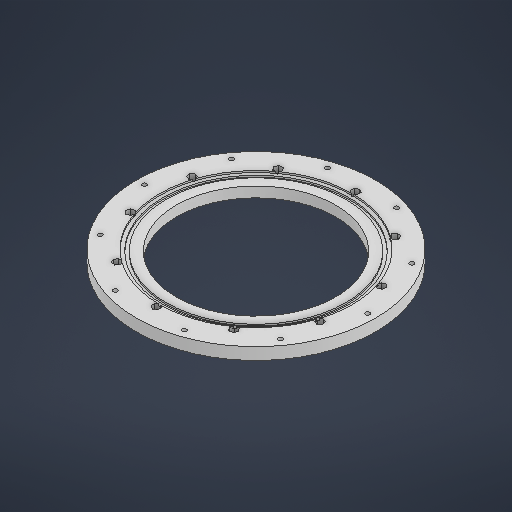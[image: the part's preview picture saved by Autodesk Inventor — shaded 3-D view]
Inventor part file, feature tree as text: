
AUTODESK INVENTOR PART (.ipt)
format: ipt  version: 2025 (Build 290162000, 162)  size: 542,720 bytes
history: native  units: in
note: dims shown in document units (in); Inventor stores cm internally (conversion verified against a paired STEP export)
features: sketch x11, extrude x5, hole x1, revolve x1
ambient origin geometry x8: Origin, YZ Plane, XZ Plane, XY Plane, X Axis, Y Axis, Z Axis, Center Point
bodies: Solid1 (feature_tree)
feature tree (18):
  sketch  "Sketch1"  dims[d0=11.811in d1=7.874in]
  extrude  "Extrusion1"  Depth=7.874in
  sketch  "Sketch2"  dims[d7=0.2165in d9=3.937in d11=360.0deg]
  extrude  "Extrusion2"  Depth=0.1969in TaperAngle=0.0deg
  sketch  "Sketch3"  dims[d13=0.3012in d14=0.0in d15=9.8425in]
  extrude  "Extrusion3"  Depth=3.937in TaperAngle=360.0deg
  extrude  "Extrusion6"  Depth=9.8425in
  extrude  "Extrusion7"  Depth=0.1575in TaperAngle=0.0deg
  hole  "Hole2"  [1 undecoded]
  revolve  "Revolution1"  [1 undecoded]
  sketch  "Sketch Circular Pattern1"  dims[d2=9.8425in d5=0.1969in d6=0.0in]
  sketch  "Sketch5"  dims[d29=9.5079in d30=0.0837in d31=0.0in]
  sketch  "Sketch6"  dims[d47=3.937in d49=360.0deg]
  sketch  "Sketch8"  dims[d58=0.1575in]
  sketch  "Sketch Circular Pattern4"  dims[d20=0.1319in d21=0.0in d27=0.1575in d28=0.0in]
  sketch  "Sketch9"  dims[d59=0.1575in d60=0.5709in d61=0.1575in d62=0.1575in d63=90.0deg d64=0.3445in d65=4.9213in d66=4.9213in d67=0.3445in d70=3.937in d72=360.0deg d74=3.937in d76=360.0deg d78=7.874in d79=7.874in d25=0.0197in d26=0.0344in]
  sketch  "Sketch Circular Pattern5"  dims[d45=11.0236in d46=0.2165in]
  sketch  "Sketch Circular Pattern6"  dims[d51=0.2165in d52=0.2362in d53=0.4124in d54=0.2904in d55=90.0deg d56=0.315in d57=0.8108in]
note: 2 required parameter values undecoded (feature->parameter linkage not recoverable at this tier; creation-order binding heuristic only, values carry confidence <= 0.55)